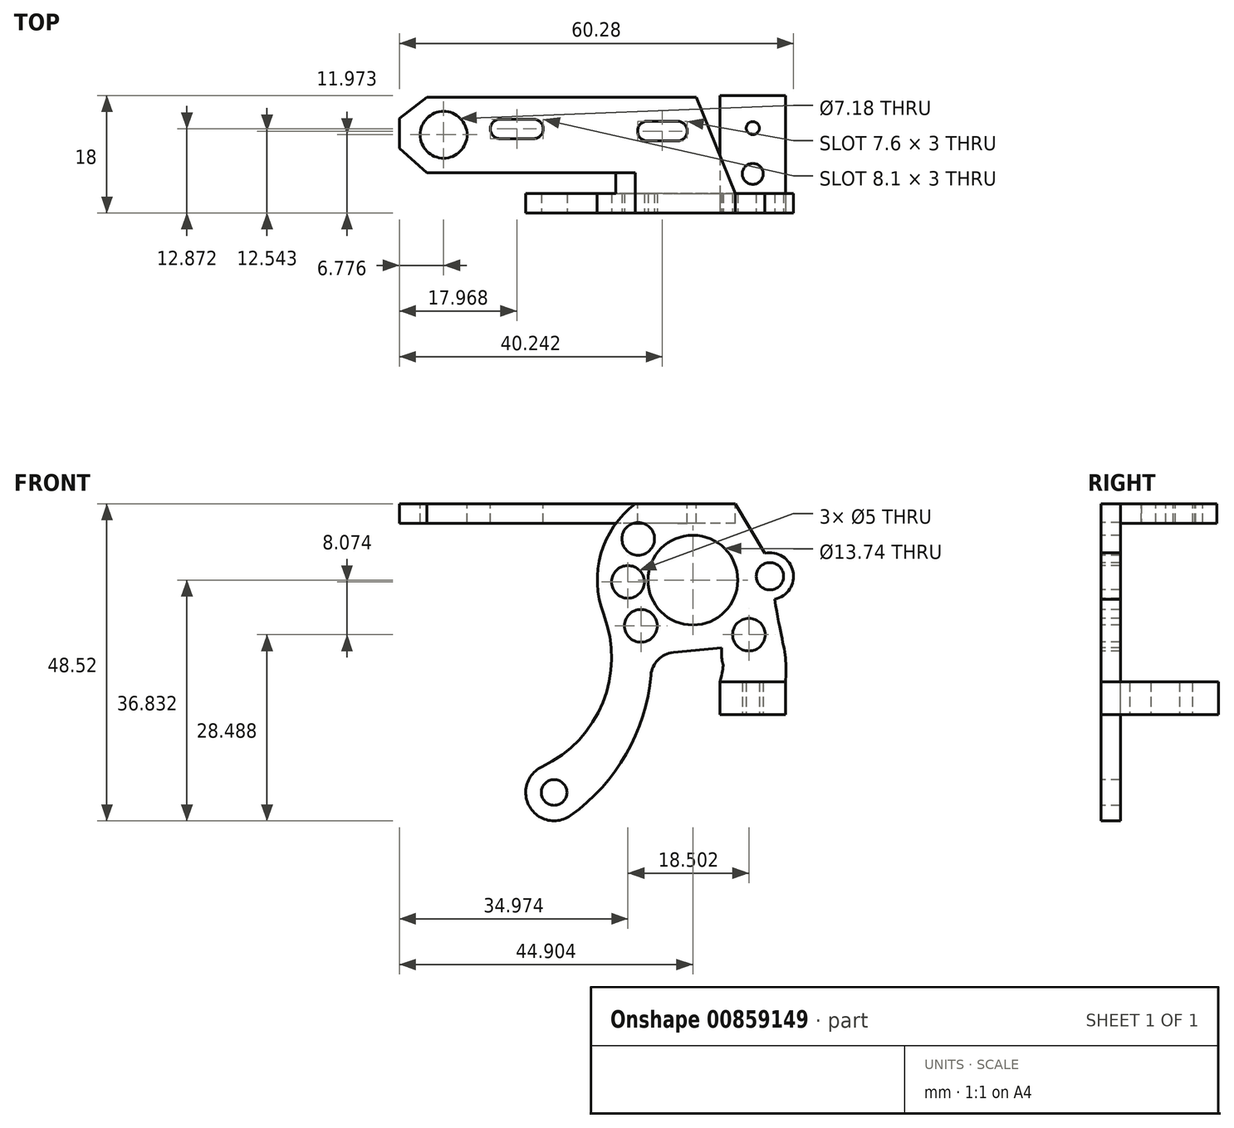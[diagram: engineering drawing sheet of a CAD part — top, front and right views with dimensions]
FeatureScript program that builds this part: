
annotation { "Feature Type Name" : "Feature", "Feature Type Description" : "" }
export const myFeature = defineFeature(function(context is Context, id is Id, definition is map)
    precondition{}
    {
        {
            var Q0;
            Q0=qCreatedBy(makeId("Top.planeOp"),FACE);
            var sketch = newSketch(context, id + "F0", { "sketchPlane" : qUnion([Q0])});
            skLineSegment(sketch, "E0.bottom", {"start": v(-13.32, 10.09) * mm, "end": v(-3.32, 10.09) * mm});
            skLineSegment(sketch, "E0.top", {"start": v(-13.32, -7.91) * mm, "end": v(-3.32, -7.91) * mm});
            skLineSegment(sketch, "E0.left", {"start": v(-13.32, 10.09) * mm, "end": v(-13.32, -7.91) * mm});
            skLineSegment(sketch, "E0.right", {"start": v(-3.32, 10.09) * mm, "end": v(-3.32, -7.91) * mm});
            skCircle(sketch, "E1", {"center": v(-8.32, -1.91) * mm, "radius": 1.6 * mm});
            skCircle(sketch, "E2", {"center": v(-8.32, 5.09) * mm, "radius": 1 * mm});
            skSolve(sketch);
        }
        {
            var Q0;
            Q0 = qSketchRegion(id + "F0", true);
            extrude(context, id + "F1", {"entities" : qUnion([Q0]), "depth" : 5 * mm, "offsetDistance" : 25 * mm});
        }
        {
            var Q0;
            Q0=makeQuery(id+"F1.opExtrude","SWEPT_FACE",FACE,{"disambiguationData":[OSD([sQuery(id+"F0.wireOp",EDGE,"E0.top")])]});
            var sketch = newSketch(context, id + "F2", { "sketchPlane" : qUnion([Q0])});
            skFitSpline(sketch, "E3", {"points": [v(-3.32, 5) * mm, v(-3.32, 8.67) * mm, v(-4.95, 17.64) * mm], "startDerivative": vector(0.52, 8.44) * mm, "endDerivative": vector(-3.36, 23.07) * mm});
            skFitSpline(sketch, "E4", {"points": [v(-13.32, 5) * mm, v(-13.1, 10.21) * mm], "startDerivative": vector(2.8, 12.89) * mm, "endDerivative": vector(0.21, 11.8) * mm});
            skArc(sketch, "E5", {"start": v(-4.95, 17.64) * mm, "mid": v(-2.19, 21.92) * mm, "end": v(-6.46, 24.68) * mm});
            skCircle(sketch, "E6", {"center": v(-5.7, 21.16) * mm, "radius": 2.09 * mm});
            skLineSegment(sketch, "E7", {"start": v(-6.46, 24.68) * mm, "end": v(-10.98, 32.26) * mm});
            skLineSegment(sketch, "E8", {"start": v(-10.98, 32.26) * mm, "end": v(-26.29, 32.26) * mm});
            skArc(sketch, "E9", {"start": v(-26.29, 32.26) * mm, "mid": v(-31.55, 24.61) * mm, "end": v(-31.15, 15.34) * mm});
            skArc(sketch, "E10", {"start": v(-31.15, 15.34) * mm, "mid": v(-31.27, 1.83) * mm, "end": v(-40.56, -8) * mm});
            skArc(sketch, "E11", {"start": v(-40.56, -8) * mm, "mid": v(-42.46, -14.12) * mm, "end": v(-36.19, -15.45) * mm});
            skArc(sketch, "E12", {"start": v(-36.19, -15.45) * mm, "mid": v(-27.7, -6.05) * mm, "end": v(-23.9, 6.04) * mm});
            skArc(sketch, "E13", {"start": v(-23.9, 6.04) * mm, "mid": v(-22.81, 8.38) * mm, "end": v(-20.48, 9.49) * mm});
            skLineSegment(sketch, "E14", {"start": v(-20.48, 9.49) * mm, "end": v(-13.1, 10.21) * mm});
            skCircle(sketch, "E15", {"center": v(-17.49, 20.57) * mm, "radius": 6.87 * mm});
            skCircle(sketch, "E16", {"center": v(-38.71, -11.92) * mm, "radius": 1.97 * mm});
            skCircle(sketch, "E17", {"center": v(-25.44, 13.58) * mm, "radius": 2.5 * mm});
            skCircle(sketch, "E18", {"center": v(-27.42, 20.3) * mm, "radius": 2.5 * mm});
            skCircle(sketch, "E19", {"center": v(-25.85, 26.89) * mm, "radius": 2.5 * mm});
            skCircle(sketch, "E20", {"center": v(-8.91, 12.23) * mm, "radius": 2.5 * mm});
            skSolve(sketch);
        }
        {
            var Q0;
            Q0=makeQuery(id+"F2.imprint","IMPRINT",FACE,{"disambiguationData":[TD([[makeQuery(id+"F2.imprint","IMPRINT",EDGE,{"derivedFrom":sQuery(id+"F2.wireOp",EDGE,"E3")}),1.0]])]});
            extrude(context, id + "F3", {"entities" : qUnion([Q0]), "oppositeDirection" : true, "depth" : 3 * mm, "offsetDistance" : 25 * mm});
        }
        {
            var Q0;
            Q0=makeQuery(id+"F3.opExtrude","SWEPT_FACE",FACE,{"disambiguationData":[OSD([sQuery(id+"F2.wireOp",EDGE,"E8")])]});
            var sketch = newSketch(context, id + "F4", { "sketchPlane" : qUnion([Q0])});
            skLineSegment(sketch, "E21", {"start": v(-10.98, -4.91) * mm, "end": v(-16.94, 9.82) * mm});
            skLineSegment(sketch, "E22", {"start": v(-16.94, 9.82) * mm, "end": v(-58.18, 9.82) * mm});
            skLineSegment(sketch, "E23", {"start": v(-62.4, 6.54) * mm, "end": v(-58.18, 9.82) * mm});
            skLineSegment(sketch, "E24", {"start": v(-62.4, 6.54) * mm, "end": v(-62.4, 1.97) * mm});
            skLineSegment(sketch, "E25", {"start": v(-62.4, 1.97) * mm, "end": v(-58.17, -1.75) * mm});
            skLineSegment(sketch, "E26", {"start": v(-58.17, -1.75) * mm, "end": v(-26.2, -1.75) * mm});
            skLineSegment(sketch, "E27", {"start": v(-26.2, -1.75) * mm, "end": v(-26.29, -4.91) * mm});
            skLineSegment(sketch, "E28", {"start": v(-26.29, -4.91) * mm, "end": v(-10.98, -4.91) * mm});
            skLineSegment(sketch, "E29", {"start": v(-19.85, 4.63) * mm, "end": v(-24.45, 4.63) * mm});
            skArc(sketch, "E30.0.startCap", {"start": v(-19.85, 6.13) * mm, "mid": v(-18.35, 4.63) * mm, "end": v(-19.85, 3.13) * mm});
            skArc(sketch, "E30.0.endCap", {"start": v(-24.45, 3.13) * mm, "mid": v(-25.95, 4.63) * mm, "end": v(-24.45, 6.13) * mm});
            skLineSegment(sketch, "E30.0.left", {"start": v(-19.85, 3.13) * mm, "end": v(-24.45, 3.13) * mm});
            skLineSegment(sketch, "E30.0.right", {"start": v(-19.85, 6.13) * mm, "end": v(-24.45, 6.13) * mm});
            skLineSegment(sketch, "E31", {"start": v(-41.87, 4.96) * mm, "end": v(-46.97, 4.96) * mm});
            skArc(sketch, "E32.0.startCap", {"start": v(-41.87, 6.46) * mm, "mid": v(-40.37, 4.96) * mm, "end": v(-41.87, 3.46) * mm});
            skArc(sketch, "E32.0.endCap", {"start": v(-46.97, 3.46) * mm, "mid": v(-48.47, 4.96) * mm, "end": v(-46.97, 6.46) * mm});
            skLineSegment(sketch, "E32.0.left", {"start": v(-41.87, 3.46) * mm, "end": v(-46.97, 3.46) * mm});
            skLineSegment(sketch, "E32.0.right", {"start": v(-41.87, 6.46) * mm, "end": v(-46.97, 6.46) * mm});
            skCircle(sketch, "E33", {"center": v(-55.61, 4.06) * mm, "radius": 3.59 * mm});
            skSolve(sketch);
        }
        {
            var Q0;
            Q0 = qSketchRegion(id + "F4", true);
            extrude(context, id + "F5", {"entities" : qUnion([Q0]), "oppositeDirection" : true, "depth" : 3 * mm, "offsetDistance" : 25 * mm});
        }
        {
            var Q0;
            Q0=makeQuery(id+"F5.opExtrude","SWEPT_FACE",FACE,{"disambiguationData":[OSD([sQuery(id+"F4.wireOp",EDGE,"E26")])]});
            var sketch = newSketch(context, id + "F6", { "sketchPlane" : qUnion([Q0])});
            skArc(sketch, "E34.0", {"start": v(-26.29, 32.26) * mm, "mid": v(-31.55, 24.61) * mm, "end": v(-31.15, 15.34) * mm});
            skLineSegment(sketch, "E35", {"start": v(-26.2, 29.26) * mm, "end": v(-29.26, 29.26) * mm});
            skLineSegment(sketch, "E36", {"start": v(-26.2, 32.26) * mm, "end": v(-26.2, 29.26) * mm});
            skSolve(sketch);
        }
        {
            var Q0;
            {var subQ4=sQuery(id+"F6.wireOp",EDGE,"E35");Q0=makeQuery(id+"F6.imprint","IMPRINT",FACE,{"disambiguationData":[TD([[makeQuery(id+"F6.imprint","IMPRINT",EDGE,{"derivedFrom":subQ4}),1.0]])]});}
            var Q1;
            Q1=makeQuery(id+"F3.opExtrude","CAP_FACE",FACE,{"disambiguationData":[OSD([sQuery(id+"F0.wireOp",EDGE,"E0.top"),sQuery(id+"F2.wireOp",EDGE,"E3"),sQuery(id+"F2.wireOp",EDGE,"E4"),sQuery(id+"F2.wireOp",EDGE,"E5"),sQuery(id+"F2.wireOp",EDGE,"E6"),sQuery(id+"F2.wireOp",EDGE,"E7"),sQuery(id+"F2.wireOp",EDGE,"E8"),sQuery(id+"F2.wireOp",EDGE,"E9"),sQuery(id+"F2.wireOp",EDGE,"E10"),sQuery(id+"F2.wireOp",EDGE,"E11"),sQuery(id+"F2.wireOp",EDGE,"E12"),sQuery(id+"F2.wireOp",EDGE,"E13"),sQuery(id+"F2.wireOp",EDGE,"E14"),sQuery(id+"F2.wireOp",EDGE,"E15"),sQuery(id+"F2.wireOp",EDGE,"E16"),sQuery(id+"F2.wireOp",EDGE,"E17"),sQuery(id+"F2.wireOp",EDGE,"E18"),sQuery(id+"F2.wireOp",EDGE,"E19"),sQuery(id+"F2.wireOp",EDGE,"E20")])],"isStart":false});
            extrude(context, id + "F7", {"entities" : qUnion([Q0]), "operationType" : NewBodyOperationType.ADD, "endBound" : BoundingType.UP_TO_SURFACE, "depth" : 25 * mm, "endBoundEntityFace" : qUnion([Q1]), "offsetDistance" : 25 * mm});
        }
    });
